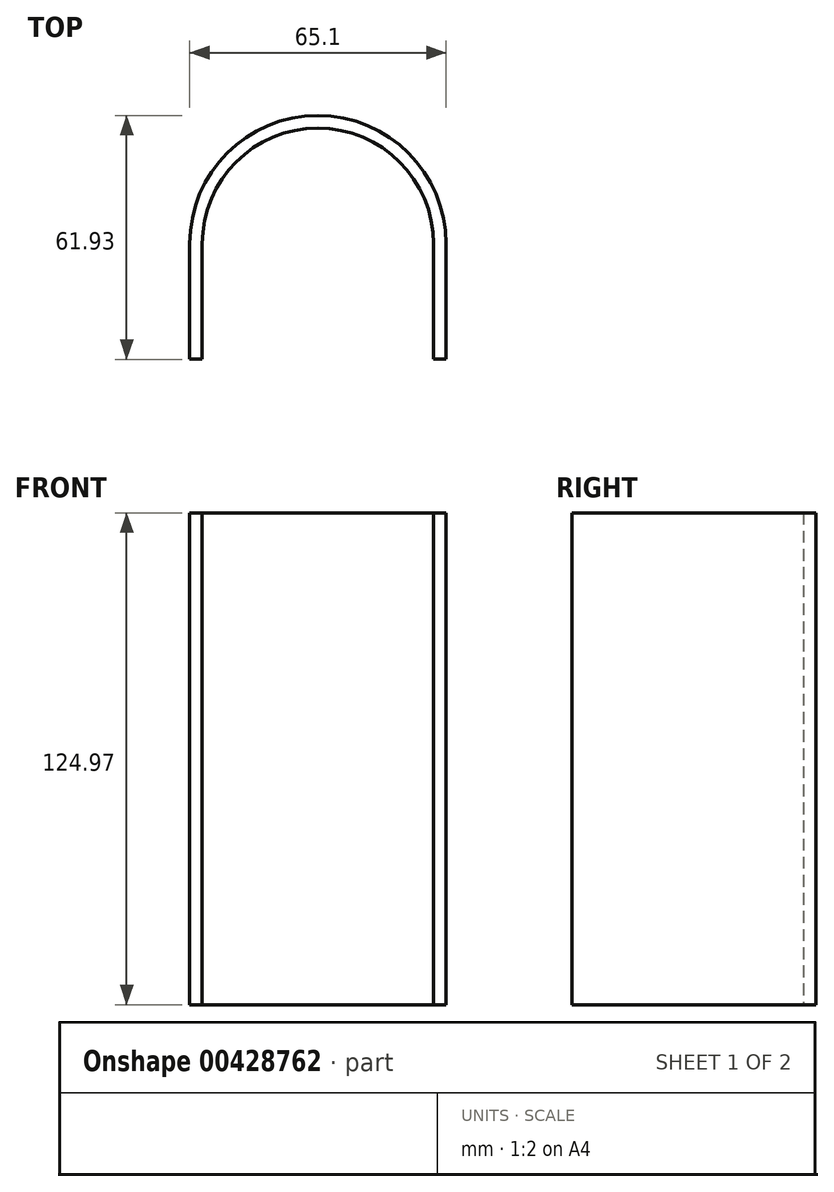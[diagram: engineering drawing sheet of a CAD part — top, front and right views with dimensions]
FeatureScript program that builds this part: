
annotation { "Feature Type Name" : "Feature", "Feature Type Description" : "" }
export const myFeature = defineFeature(function(context is Context, id is Id, definition is map)
    precondition{}
    {
        {
            var Q0;
            Q0=qCreatedBy(makeId("Top.planeOp"),FACE);
            var sketch = newSketch(context, id + "F0", { "sketchPlane" : qUnion([Q0])});
            skCircle(sketch, "E0", {"center": v(0, 0) * mm, "radius": 19.85 * mm, "construction": true});
            skArc(sketch, "E1.0", {"start": v(29.38, 0) * mm, "mid": v(0, 29.38) * mm, "end": v(-29.38, 0) * mm});
            skLineSegment(sketch, "E2", {"start": v(29.38, 0) * mm, "end": v(29.38, -29.38) * mm});
            skLineSegment(sketch, "E3", {"start": v(-29.38, 0) * mm, "end": v(-29.38, -29.38) * mm});
            skArc(sketch, "E4.0", {"start": v(32.55, 0) * mm, "mid": v(0, 32.55) * mm, "end": v(-32.55, 0) * mm});
            skLineSegment(sketch, "E5", {"start": v(29.38, -29.38) * mm, "end": v(32.55, -29.38) * mm});
            skLineSegment(sketch, "E6", {"start": v(-32.55, 0) * mm, "end": v(-32.55, -29.38) * mm});
            skLineSegment(sketch, "E7", {"start": v(-32.55, -29.38) * mm, "end": v(-29.38, -29.38) * mm});
            skLineSegment(sketch, "E8", {"start": v(-84.54, -19.85) * mm, "end": v(72.77, -19.85) * mm, "construction": true});
            skLineSegment(sketch, "E9", {"start": v(32.55, 0) * mm, "end": v(32.55, -29.38) * mm});
            skSolve(sketch);
        }
        {
            var Q0;
            Q0 = qSketchRegion(id + "F0", true);
            extrude(context, id + "F1", {"entities" : qUnion([Q0]), "depth" : 124.97 * mm});
        }
    });
